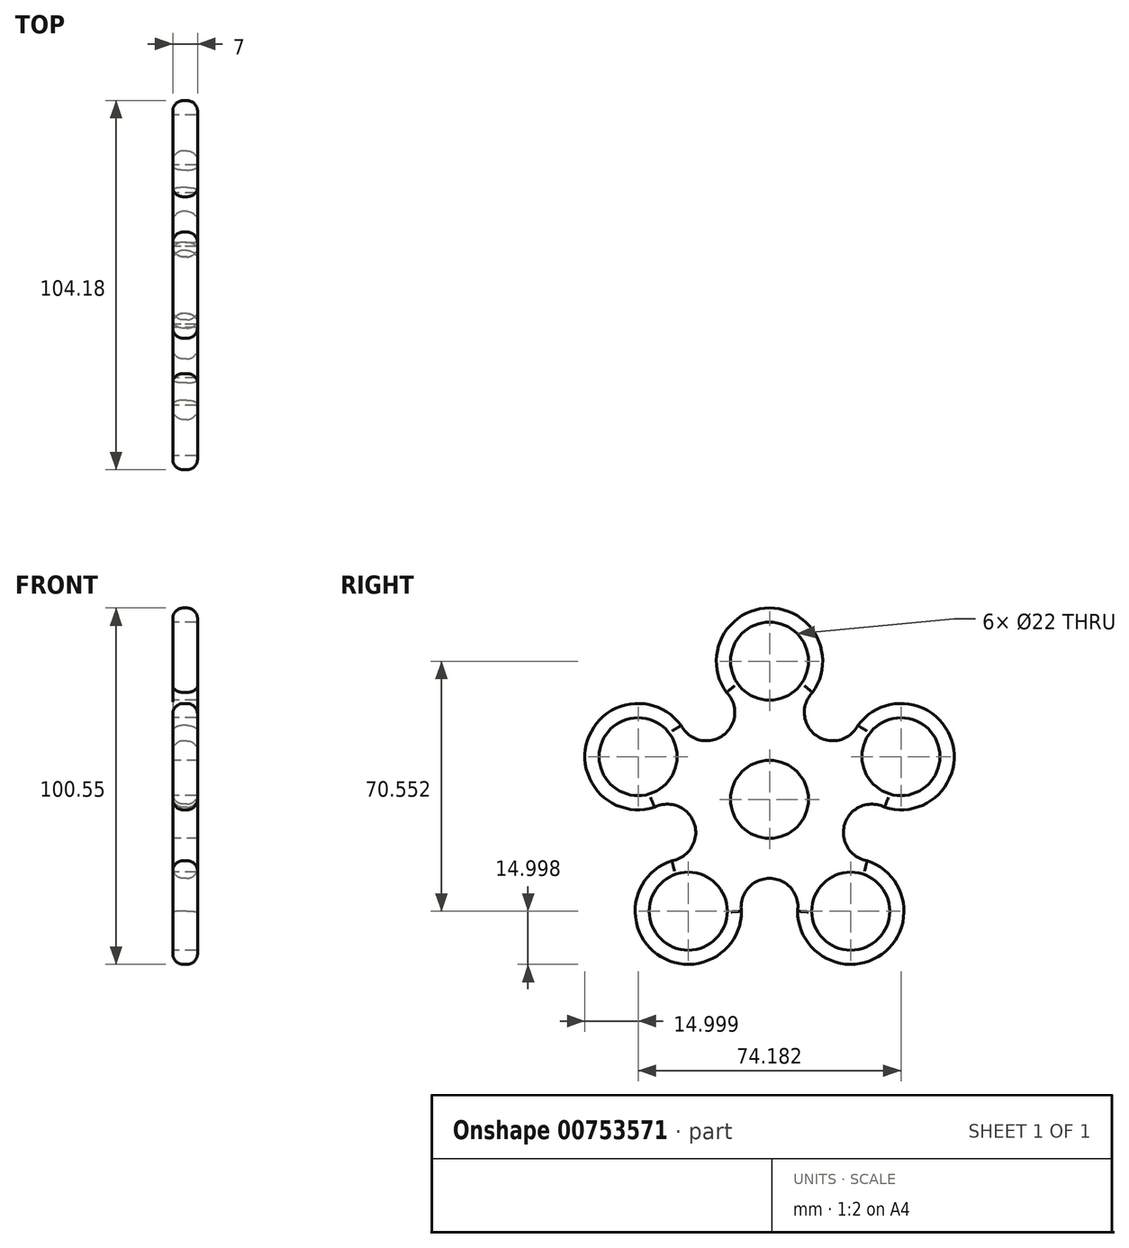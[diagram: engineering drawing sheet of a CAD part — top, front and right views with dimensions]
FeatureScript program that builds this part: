
annotation { "Feature Type Name" : "Feature", "Feature Type Description" : "" }
export const myFeature = defineFeature(function(context is Context, id is Id, definition is map)
    precondition{}
    {
        {
            var Q0;
            Q0=qCreatedBy(makeId("Right.planeOp"),FACE);
            var sketch = newSketch(context, id + "F0", { "sketchPlane" : qUnion([Q0])});
            skLineSegment(sketch, "E0", {"start": v(0, 0) * mm, "end": v(0, 39) * mm});
            skPoint(sketch, "E1.center", {"position": v(0, 0) * mm});
            skCircle(sketch, "E2", {"center": v(0, 39) * mm, "radius": 15 * mm});
            skCircle(sketch, "E3.1.0", {"center": v(-37.1, 12.05) * mm, "radius": 15 * mm});
            skCircle(sketch, "E3.2.0", {"center": v(-22.92, -31.55) * mm, "radius": 15 * mm});
            skCircle(sketch, "E3.3.0", {"center": v(22.92, -31.55) * mm, "radius": 15 * mm});
            skCircle(sketch, "E3.4.0", {"center": v(37.1, 12.05) * mm, "radius": 15 * mm});
            skArc(sketch, "E4", {"start": v(12.14, 30.18) * mm, "mid": v(13.12, 18.05) * mm, "end": v(24.96, 20.87) * mm});
            skArc(sketch, "E5.1.0", {"start": v(-24.96, 20.87) * mm, "mid": v(-13.12, 18.05) * mm, "end": v(-12.14, 30.18) * mm});
            skArc(sketch, "E5.2.0", {"start": v(-27.56, -17.29) * mm, "mid": v(-21.22, -6.9) * mm, "end": v(-32.46, -2.21) * mm});
            skArc(sketch, "E5.3.0", {"start": v(7.92, -31.55) * mm, "mid": v(0, -22.31) * mm, "end": v(-7.92, -31.55) * mm});
            skArc(sketch, "E5.4.0", {"start": v(32.46, -2.21) * mm, "mid": v(21.22, -6.9) * mm, "end": v(27.56, -17.29) * mm});
            skCircle(sketch, "E6", {"center": v(-37.1, 12.05) * mm, "radius": 11 * mm});
            skCircle(sketch, "E7.1.0", {"center": v(-22.92, -31.55) * mm, "radius": 11 * mm});
            skCircle(sketch, "E7.2.0", {"center": v(22.92, -31.55) * mm, "radius": 11 * mm});
            skCircle(sketch, "E7.3.0", {"center": v(37.1, 12.05) * mm, "radius": 11 * mm});
            skCircle(sketch, "E7.4.0", {"center": v(0, 39) * mm, "radius": 11 * mm});
            skSolve(sketch);
        }
        {
            var Q0;
            {var subQ6=sQuery(id+"F0.wireOp",EDGE,"E2");var subQ16=makeQuery(id+"F0.imprint","IMPRINT",VERTEX,{"derivedFrom":subQ6});Q0=makeQuery(id+"F0.imprint","IMPRINT",FACE,{"disambiguationData":[TD([[makeQuery(id+"F0.imprint","IMPRINT",EDGE,{"disambiguationData":[TD([[subQ16,1.0]])],"derivedFrom":subQ6}),-1.0]])]});}
            var Q1;
            Q1=makeQuery(id+"F0.imprint","IMPRINT",FACE,{"disambiguationData":[TD([[makeQuery(id+"F0.imprint","IMPRINT",EDGE,{"derivedFrom":sQuery(id+"F0.wireOp",EDGE,"E7.3.0")}),-1.0]])]});
            var Q2;
            Q2=makeQuery(id+"F0.imprint","IMPRINT",FACE,{"disambiguationData":[TD([[makeQuery(id+"F0.imprint","IMPRINT",EDGE,{"derivedFrom":sQuery(id+"F0.wireOp",EDGE,"E7.2.0")}),-1.0]])]});
            var Q3;
            Q3=makeQuery(id+"F0.imprint","IMPRINT",FACE,{"disambiguationData":[TD([[makeQuery(id+"F0.imprint","IMPRINT",EDGE,{"derivedFrom":sQuery(id+"F0.wireOp",EDGE,"E7.1.0")}),-1.0]])]});
            var Q4;
            Q4=makeQuery(id+"F0.imprint","IMPRINT",FACE,{"disambiguationData":[TD([[makeQuery(id+"F0.imprint","IMPRINT",EDGE,{"derivedFrom":sQuery(id+"F0.wireOp",EDGE,"E6")}),-1.0]])]});
            var Q5;
            Q5=makeQuery(id+"F0.imprint","IMPRINT",FACE,{"disambiguationData":[TD([[makeQuery(id+"F0.imprint","IMPRINT",EDGE,{"derivedFrom":sQuery(id+"F0.wireOp",EDGE,"E7.4.0")}),-1.0]])]});
            extrude(context, id + "F1", {"entities" : qUnion([Q0, Q1, Q2, Q3, Q4, Q5]), "depth" : 7 * mm, "offsetDistance" : 25.4 * mm});
        }
        {
            var Q0;
            Q0=makeQuery(id+"F1.opExtrude","CAP_EDGE",EDGE,{"disambiguationData":[OSD([sQuery(id+"F0.wireOp",EDGE,"E3.1.0")])],"isStart":false});
            var Q1;
            Q1=makeQuery(id+"F1.opExtrude","CAP_EDGE",EDGE,{"disambiguationData":[OSD([sQuery(id+"F0.wireOp",EDGE,"E5.1.0")])],"isStart":false});
            var Q2;
            Q2=makeQuery(id+"F1.opExtrude","CAP_EDGE",EDGE,{"disambiguationData":[OSD([sQuery(id+"F0.wireOp",EDGE,"E2")])],"isStart":false});
            var Q3;
            Q3=makeQuery(id+"F1.opExtrude","CAP_EDGE",EDGE,{"disambiguationData":[OSD([sQuery(id+"F0.wireOp",EDGE,"E4")])],"isStart":false});
            var Q4;
            Q4=makeQuery(id+"F1.opExtrude","CAP_EDGE",EDGE,{"disambiguationData":[OSD([sQuery(id+"F0.wireOp",EDGE,"E3.4.0")])],"isStart":false});
            var Q5;
            Q5=makeQuery(id+"F1.opExtrude","CAP_EDGE",EDGE,{"disambiguationData":[OSD([sQuery(id+"F0.wireOp",EDGE,"E5.4.0")])],"isStart":false});
            var Q6;
            Q6=makeQuery(id+"F1.opExtrude","CAP_EDGE",EDGE,{"disambiguationData":[OSD([sQuery(id+"F0.wireOp",EDGE,"E3.3.0")])],"isStart":false});
            var Q7;
            Q7=makeQuery(id+"F1.opExtrude","CAP_EDGE",EDGE,{"disambiguationData":[OSD([sQuery(id+"F0.wireOp",EDGE,"E5.3.0")])],"isStart":false});
            var Q8;
            Q8=makeQuery(id+"F1.opExtrude","CAP_EDGE",EDGE,{"disambiguationData":[OSD([sQuery(id+"F0.wireOp",EDGE,"E3.2.0")])],"isStart":false});
            var Q9;
            Q9=makeQuery(id+"F1.opExtrude","CAP_EDGE",EDGE,{"disambiguationData":[OSD([sQuery(id+"F0.wireOp",EDGE,"E5.2.0")])],"isStart":false});
            var Q10;
            Q10=makeQuery(id+"F1.opExtrude","CAP_EDGE",EDGE,{"disambiguationData":[OSD([sQuery(id+"F0.wireOp",EDGE,"E3.4.0")])],"isStart":true});
            var Q11;
            Q11=makeQuery(id+"F1.opExtrude","CAP_EDGE",EDGE,{"disambiguationData":[OSD([sQuery(id+"F0.wireOp",EDGE,"E5.4.0")])],"isStart":true});
            var Q12;
            Q12=makeQuery(id+"F1.opExtrude","CAP_EDGE",EDGE,{"disambiguationData":[OSD([sQuery(id+"F0.wireOp",EDGE,"E3.3.0")])],"isStart":true});
            var Q13;
            Q13=makeQuery(id+"F1.opExtrude","CAP_EDGE",EDGE,{"disambiguationData":[OSD([sQuery(id+"F0.wireOp",EDGE,"E5.3.0")])],"isStart":true});
            var Q14;
            Q14=makeQuery(id+"F1.opExtrude","CAP_EDGE",EDGE,{"disambiguationData":[OSD([sQuery(id+"F0.wireOp",EDGE,"E3.2.0")])],"isStart":true});
            var Q15;
            Q15=makeQuery(id+"F1.opExtrude","CAP_EDGE",EDGE,{"disambiguationData":[OSD([sQuery(id+"F0.wireOp",EDGE,"E5.2.0")])],"isStart":true});
            var Q16;
            Q16=makeQuery(id+"F1.opExtrude","CAP_EDGE",EDGE,{"disambiguationData":[OSD([sQuery(id+"F0.wireOp",EDGE,"E3.1.0")])],"isStart":true});
            var Q17;
            Q17=makeQuery(id+"F1.opExtrude","CAP_EDGE",EDGE,{"disambiguationData":[OSD([sQuery(id+"F0.wireOp",EDGE,"E5.1.0")])],"isStart":true});
            var Q18;
            Q18=makeQuery(id+"F1.opExtrude","CAP_EDGE",EDGE,{"disambiguationData":[OSD([sQuery(id+"F0.wireOp",EDGE,"E2")])],"isStart":true});
            var Q19;
            Q19=makeQuery(id+"F1.opExtrude","CAP_EDGE",EDGE,{"disambiguationData":[OSD([sQuery(id+"F0.wireOp",EDGE,"E4")])],"isStart":true});
            fillet(context, id + "F2", {"entities" : qUnion([Q0, Q1, Q2, Q3, Q4, Q5, Q6, Q7, Q8, Q9, Q10, Q11, Q12, Q13, Q14, Q15, Q16, Q17, Q18, Q19]), "radius" : 3 * mm, "tangentPropagation" : true, "allowEdgeOverflow" : false});
        }
        {
            var Q0;
            Q0=qCreatedBy(makeId("Right.planeOp"),FACE);
            var sketch = newSketch(context, id + "F3", { "sketchPlane" : qUnion([Q0])});
            skCircle(sketch, "E8", {"center": v(0, 0) * mm, "radius": 11 * mm});
            skSolve(sketch);
        }
        {
            var Q0;
            Q0=makeQuery(id+"F3.imprint","IMPRINT",FACE,{"disambiguationData":[TD([[makeQuery(id+"F3.imprint","IMPRINT",EDGE,{"derivedFrom":sQuery(id+"F3.wireOp",EDGE,"E8")}),1.0]])]});
            extrude(context, id + "F4", {"entities" : qUnion([Q0]), "operationType" : NewBodyOperationType.REMOVE, "depth" : 7 * mm, "offsetDistance" : 25.4 * mm});
        }
        {
            var Q0;
            Q0=makeQuery(id+"F1.opExtrude","CAP_EDGE",EDGE,{"disambiguationData":[OSD([sQuery(id+"F0.wireOp",EDGE,"E7.4.0")])],"isStart":true});
            var Q1;
            Q1=makeQuery(id+"F4.boolean.opBoolean","COPY",EDGE,{"derivedFrom":makeQuery(id+"F4.opExtrude","CAP_EDGE",EDGE,{"disambiguationData":[OSD([sQuery(id+"F3.wireOp",EDGE,"E8")])],"isStart":true})});
            var Q2;
            Q2=makeQuery(id+"F1.opExtrude","CAP_EDGE",EDGE,{"disambiguationData":[OSD([sQuery(id+"F0.wireOp",EDGE,"E7.3.0")])],"isStart":true});
            var Q3;
            Q3=makeQuery(id+"F1.opExtrude","CAP_EDGE",EDGE,{"disambiguationData":[OSD([sQuery(id+"F0.wireOp",EDGE,"E7.2.0")])],"isStart":true});
            var Q4;
            Q4=makeQuery(id+"F1.opExtrude","CAP_EDGE",EDGE,{"disambiguationData":[OSD([sQuery(id+"F0.wireOp",EDGE,"E7.1.0")])],"isStart":true});
            var Q5;
            Q5=makeQuery(id+"F1.opExtrude","CAP_EDGE",EDGE,{"disambiguationData":[OSD([sQuery(id+"F0.wireOp",EDGE,"E6")])],"isStart":true});
            var Q6;
            Q6=makeQuery(id+"F1.opExtrude","CAP_EDGE",EDGE,{"disambiguationData":[OSD([sQuery(id+"F0.wireOp",EDGE,"E6")])],"isStart":false});
            var Q7;
            Q7=makeQuery(id+"F1.opExtrude","CAP_EDGE",EDGE,{"disambiguationData":[OSD([sQuery(id+"F0.wireOp",EDGE,"E7.4.0")])],"isStart":false});
            var Q8;
            Q8=makeQuery(id+"F1.opExtrude","CAP_EDGE",EDGE,{"disambiguationData":[OSD([sQuery(id+"F0.wireOp",EDGE,"E7.3.0")])],"isStart":false});
            var Q9;
            {var subQ0=sQuery(id+"F0.wireOp",EDGE,"E3.3.0");Q9=makeQuery(id+"F2.opFillet","BLEND_EDGE",EDGE,{"blendedFrom":[makeQuery(id+"F1.opExtrude","CAP_EDGE",EDGE,{"disambiguationData":[OSD([subQ0])],"isStart":false}),makeQuery(id+"F1.opExtrude","CAP_FACE",FACE,{"disambiguationData":[OSD([sQuery(id+"F0.wireOp",EDGE,"E2"),sQuery(id+"F0.wireOp",EDGE,"E3.1.0"),sQuery(id+"F0.wireOp",EDGE,"E3.2.0"),subQ0,sQuery(id+"F0.wireOp",EDGE,"E3.4.0"),sQuery(id+"F0.wireOp",EDGE,"E4"),sQuery(id+"F0.wireOp",EDGE,"E5.1.0"),sQuery(id+"F0.wireOp",EDGE,"E5.2.0"),sQuery(id+"F0.wireOp",EDGE,"E5.3.0"),sQuery(id+"F0.wireOp",EDGE,"E5.4.0"),sQuery(id+"F0.wireOp",EDGE,"E6"),sQuery(id+"F0.wireOp",EDGE,"E7.1.0"),sQuery(id+"F0.wireOp",EDGE,"E7.2.0"),sQuery(id+"F0.wireOp",EDGE,"E7.3.0"),sQuery(id+"F0.wireOp",EDGE,"E7.4.0")])],"isStart":false})],"blendedInto":[makeQuery(id+"F1.opExtrude","CAP_FACE",FACE,{"disambiguationData":[OSD([sQuery(id+"F0.wireOp",EDGE,"E2"),sQuery(id+"F0.wireOp",EDGE,"E3.1.0"),sQuery(id+"F0.wireOp",EDGE,"E3.2.0"),subQ0,sQuery(id+"F0.wireOp",EDGE,"E3.4.0"),sQuery(id+"F0.wireOp",EDGE,"E4"),sQuery(id+"F0.wireOp",EDGE,"E5.1.0"),sQuery(id+"F0.wireOp",EDGE,"E5.2.0"),sQuery(id+"F0.wireOp",EDGE,"E5.3.0"),sQuery(id+"F0.wireOp",EDGE,"E5.4.0"),sQuery(id+"F0.wireOp",EDGE,"E6"),sQuery(id+"F0.wireOp",EDGE,"E7.1.0"),sQuery(id+"F0.wireOp",EDGE,"E7.2.0"),sQuery(id+"F0.wireOp",EDGE,"E7.3.0"),sQuery(id+"F0.wireOp",EDGE,"E7.4.0")])],"isStart":false})]});}
            var Q10;
            Q10=makeQuery(id+"F4.boolean.opBoolean","COPY",EDGE,{"derivedFrom":makeQuery(id+"F4.opExtrude","CAP_EDGE",EDGE,{"disambiguationData":[OSD([sQuery(id+"F3.wireOp",EDGE,"E8")])],"isStart":false})});
            var Q11;
            Q11=makeQuery(id+"F1.opExtrude","CAP_EDGE",EDGE,{"disambiguationData":[OSD([sQuery(id+"F0.wireOp",EDGE,"E7.1.0")])],"isStart":false});
            var Q12;
            Q12=makeQuery(id+"F1.opExtrude","CAP_EDGE",EDGE,{"disambiguationData":[OSD([sQuery(id+"F0.wireOp",EDGE,"E7.2.0")])],"isStart":false});
            fillet(context, id + "F5", {"entities" : qUnion([Q0, Q1, Q2, Q3, Q4, Q5, Q6, Q7, Q8, Q9, Q10, Q11, Q12]), "radius" : 0.5 * mm, "tangentPropagation" : true, "allowEdgeOverflow" : false});
        }
    });
